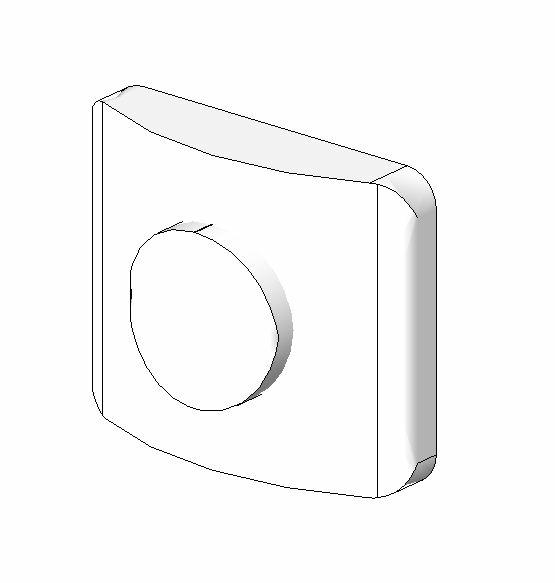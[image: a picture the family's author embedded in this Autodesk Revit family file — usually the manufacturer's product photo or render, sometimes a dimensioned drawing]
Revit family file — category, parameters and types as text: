
# Revit family: Deca_Valvula de descarga_Hydra Eco_2565.CONF
name_source: partatom
category: Plumbing Fixtures
units: mm (PartAtom-declared; Revit-internal decimal feet)

## family parameters
Cut with Voids When Loaded = No
Host = Face
Part Type = Normal
Room Calculation Point = No
Round Connector Dimension = Use Radius
Shared = No

## types (2) — shared parameters
Acompanha o Produto = -
Aprovado por = quattroD
Atendimento ao Cliente = 0800-0117073
CW Connection = No
Categoria = SISTEMAS DE DESCARGA
Composição Anel Vedação = -
Composição Assento = -
Composição Básica = Liga de Cobre (bronze e latão),Plásticos de Engenharia,Elastômeros
Composição Componente = -
Cor Interna = -
Cor Principal = Cromado
Cor Secundária = -
Cores Componente = -
Criado por = quattroD
Código Pai = 2565.CONF
Default Elevation = 1100 mm
Diâmetro Água Fria Saída = 40 mm  [stored 0.131234 ft]
Informações Complementares = -
Itens de Instalação = -
Linha = Hydra Eco
Manufacturer = Deca
Material = Deca_Cromado
Norma = NBR15857;NBR9050
Pressão mín. Aquec. Acúmulo = -
Pressão mín. Aquec. Passagem = -
Raio Água Fria Saída = 20 mm  [stored 0.0656168 ft]
Saída de Esgoto = -
Segmento = Válvula Hydra
Tipo de dispositivo economizador = -
Tipo de mecanismo utilizado = -
Tipo de rosca de entrada = BSP NBR 8133
Tipo de rosca de saída = BSP NBR 8133
URL = www.deca.com.br
Vazão na Pressão máx. (L/min) = -
Vazão na Pressão mín. (L/min) = -
zero-valued in all types: CWFU

## per-type parameters (varying)
| type | Consumo | Description | Diâmetro Água Fria | Model | Peso Líquido (Kg) | Pressão máx. funcionamento | Pressão mín. funcionamento | Raio Água Fria |
| 2565.C.112.CONF_Cromado_DN40 | 6 lpf | Válvula de descarga 1 1/2" | 40 mm  [stored 0.131234 ft] | 2565.C.112.CONF | 1.412 | 10 MCA | 2 MCA | 20 mm  [stored 0.0656168 ft] |
| 2565.C.114.CONF_Cromado_DN32 | 6lpf | Válvula de descarga 1 1/4" | 32 mm  [stored 0.104987 ft] | 2565.C.114.CONF | 1.443 | 40 MCA | 10 MCA | 16 mm  [stored 0.0524934 ft] |

note: [stored X ft] marks values corroborated as IEEE doubles in the binary element streams (Revit-internal decimal feet)

## geometry (parser evidence)
native form markers: Sweep x3
no freeform markers — native parametric forms only
